# Revit family: Power-ModularDevices-GEWISS-90AM-TRANSFORMER_BELL_3M
name_source: partatom
category: Apparecchi elettrici
revit_build: Autodesk Revit 2016 (Build: 20161004_0715(x64)
units: mm (PartAtom-declared; Revit-internal decimal feet)

## family parameters
Condiviso = No
Host = Superficie
Mantenere orientamento annotazione = Sì
Numero OmniClass = 23.80.50.00
Punto di calcolo locali = Sì
Quota connettore circolare = Usa diametro
Taglio con vuoti quando caricato = No
Tipo di parte = Normale
Titolo OmniClass = Terminals for Power Supply

## types (4) — shared parameters
Catalogue = POWER
Catalogue Range = 90 AM
Electrocod = 140
IDF = 4f95a082-cf0f-486c-8155-70e44cc748f8
IDT = be1f04d5-2035-480f-a688-5e0ac10cfa0d
Immagine tipo = GW96433.jpg
No. Chorus modules = 3
No. of modules EN 50022 = 3
Numero di poli = 1
Operation = Intermittent
Primary voltage = 230V
Produttore = GEWISS S.p.A.
Prospetto di default = 1219 mm
SEO = Transformer
Spostamento_x = -3300 mm  [stored -10.8268 ft]
Technical sheet = https://www.gewiss.com
URL = https://www.gewiss.com
Version file RFA = 18.0
carico = Altro
potenza in watt = 0 V
zero-valued in all types: Barra_DIN

## per-type parameters (varying)
| type | Descrizione | EAN code | Modello | Power | Rated power: | Secondary voltage |
| GW96433 - BELL TRANSFORMER 40VA T.P.230V T.S.12V | BELL TRANSFORMER 40VA T.P.230V T.S.12V | 8011564063785 | GW96433 | 40VA (12V)/27VA (8V)/13VA (4V) | 40 VA (12 V)/27 VA (8 V)/13 VA (4 V) | 4+8=12 V |
| GW96432 - BELL TRANSFORMER 30VA T.P.230V T.S.24V | BELL TRANSFORMER 30VA T.P.230V T.S.24V | 8011564063778 | GW96432 | 30VA (24V)/15VA (12V) | 30 VA (24 V)/15 VA (12 V) | 12+12=24 V |
| GW96431 - BELL TRANSFORMER 30VA T.P.230V T.S.12V | BELL TRANSFORMER 30VA T.P.230V T.S.12V | 8011564063761 | GW96431 | 30VA (12V)/20VA (8V)/10VA (4V) | 30 VA (12 V)/20 VA (8 V)/10 VA (4 V) | 4+8=12 V |
| GW96434 - BELL TRANSFORMER 40VA T.P.230V T.S.24V | BELL TRANSFORMER 40VA T.P.230V T.S.24V | 8011564063792 | GW96434 | 40VA (24V)/20VA (12V) | 40 VA (24 V)/20 VA (12 V) | 12+12=24 V |

note: [stored X ft] marks values corroborated as IEEE doubles in the binary element streams (Revit-internal decimal feet)
